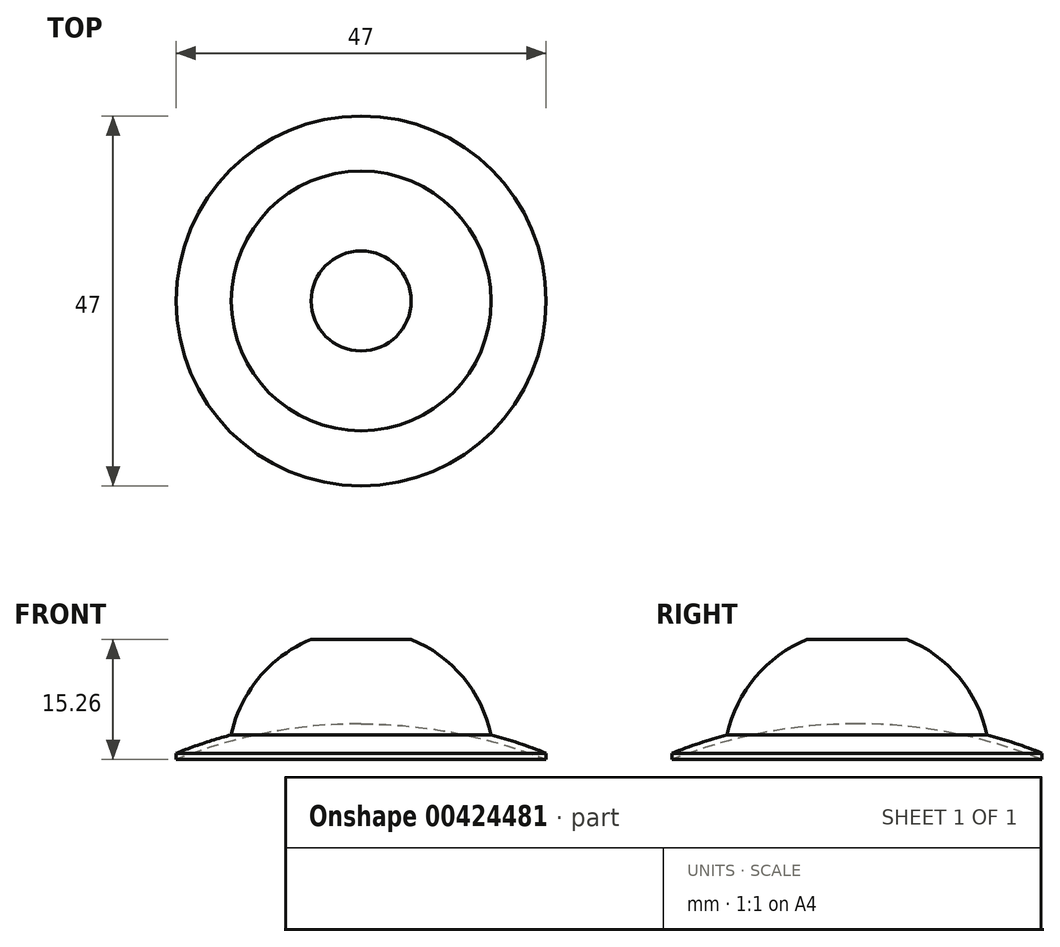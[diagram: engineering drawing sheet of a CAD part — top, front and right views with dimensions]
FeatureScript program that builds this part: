
annotation { "Feature Type Name" : "Feature", "Feature Type Description" : "" }
export const myFeature = defineFeature(function(context is Context, id is Id, definition is map)
    precondition{}
    {
        {
            var Q0;
            Q0=qCreatedBy(makeId("Front.planeOp"),FACE);
            var sketch = newSketch(context, id + "F0", { "sketchPlane" : qUnion([Q0])});
            skArc(sketch, "E0", {"start": v(0, -3.71) * mm, "mid": v(-11.97, -4.86) * mm, "end": v(-23.5, -8.25) * mm});
            skLineSegment(sketch, "E1", {"start": v(0, -3.71) * mm, "end": v(0, 7.03) * mm});
            skLineSegment(sketch, "E2", {"start": v(-23.5, -8.25) * mm, "end": v(-23.5, -7.45) * mm});
            skArc(sketch, "E3", {"start": v(-16.5, -5.11) * mm, "mid": v(-20.03, -6.18) * mm, "end": v(-23.5, -7.45) * mm});
            skLineSegment(sketch, "E4", {"start": v(-6.35, 7.01) * mm, "end": v(0, 7.01) * mm});
            skArc(sketch, "E5.trimOffspring", {"start": v(-6.35, 7.01) * mm, "mid": v(-12.93, 2.21) * mm, "end": v(-16.5, -5.11) * mm});
            skSolve(sketch);
        }
        {
            var Q0;
            Q0 = qSketchRegion(id + "F0", true);
            var Q1;
            Q1=sQuery(id+"F0.wireOp",EDGE,"E1");
            revolve(context, id + "F1", {"surfaceOperationType" : NewSurfaceOperationType.NEW, "entities" : qUnion([Q0]), "axis" : qUnion([Q1]), "revolveType" : RevolveType.FULL});
        }
    });
